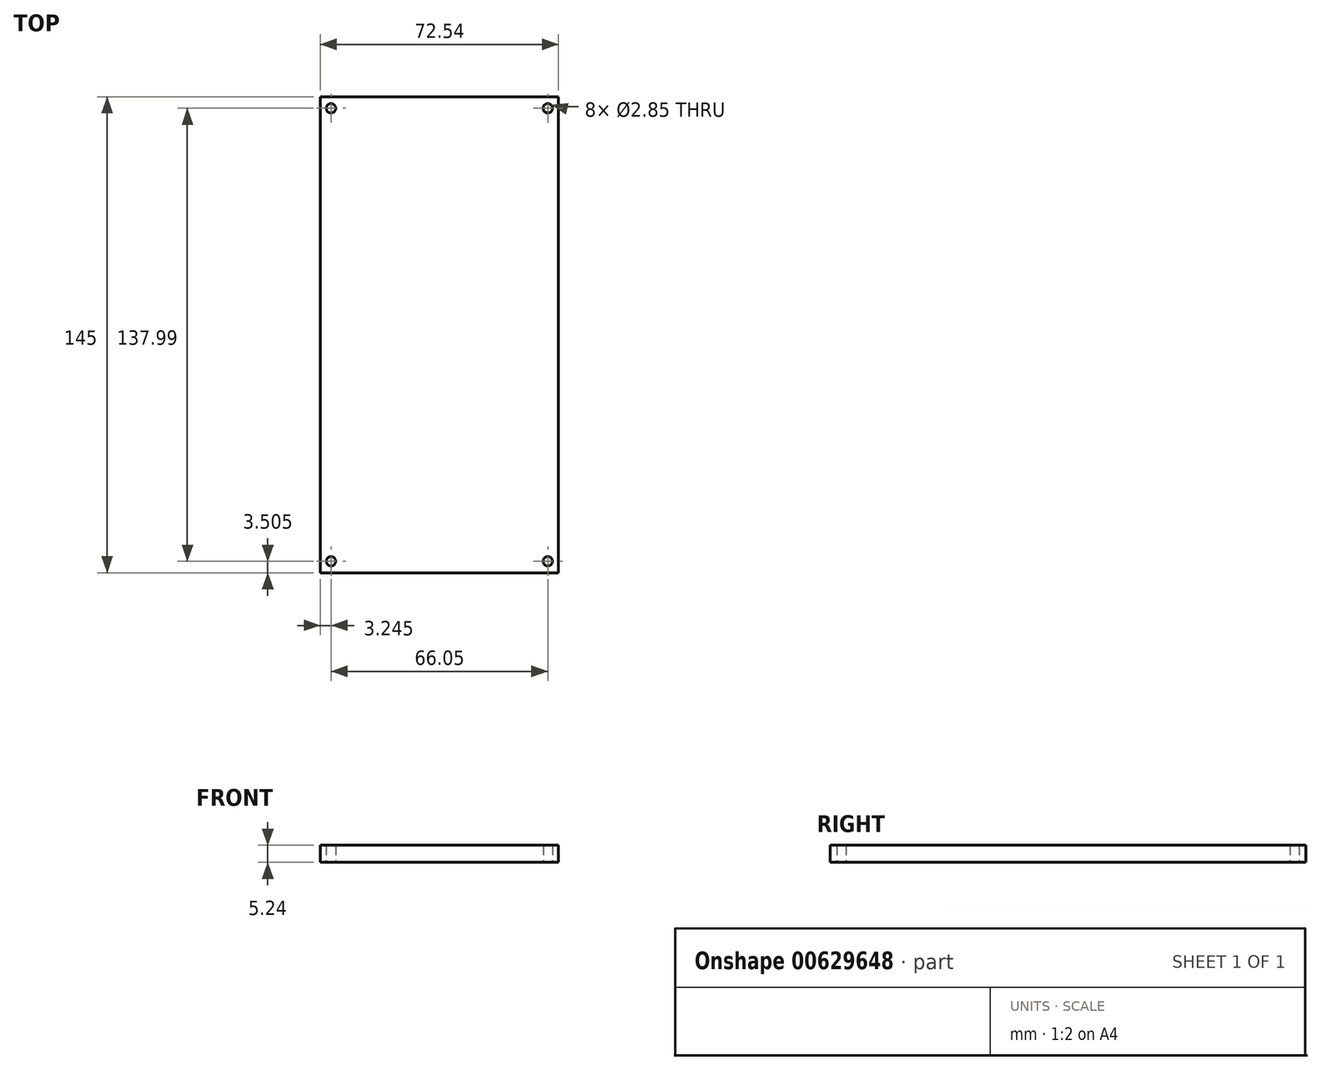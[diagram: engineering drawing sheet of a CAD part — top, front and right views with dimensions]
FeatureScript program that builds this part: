
annotation { "Feature Type Name" : "Feature", "Feature Type Description" : "" }
export const myFeature = defineFeature(function(context is Context, id is Id, definition is map)
    precondition{}
    {
        {
            var Q0;
            Q0=qCreatedBy(makeId("Top.planeOp"),FACE);
            var sketch = newSketch(context, id + "F0", { "sketchPlane" : qUnion([Q0])});
            skLineSegment(sketch, "E0.bottom", {"start": v(-36.27, -72.5) * mm, "end": v(-36.27, 72.5) * mm});
            skLineSegment(sketch, "E0.top", {"start": v(36.27, -72.5) * mm, "end": v(36.27, 72.5) * mm});
            skLineSegment(sketch, "E0.left", {"start": v(-36.27, -72.5) * mm, "end": v(36.27, -72.5) * mm});
            skLineSegment(sketch, "E0.right", {"start": v(-36.27, 72.5) * mm, "end": v(36.27, 72.5) * mm});
            skPoint(sketch, "E0.middle", {"position": v(0, 0) * mm});
            skPoint(sketch, "E1", {"position": v(0, 72.5) * mm});
            skPoint(sketch, "E2", {"position": v(36.27, 0) * mm});
            skCircle(sketch, "E3", {"center": v(33.03, 69) * mm, "radius": 1.43 * mm});
            skCircle(sketch, "E4", {"center": v(-33.03, 69) * mm, "radius": 1.43 * mm});
            skCircle(sketch, "E5", {"center": v(33.03, -69) * mm, "radius": 1.43 * mm});
            skCircle(sketch, "E6", {"center": v(-33.03, -69) * mm, "radius": 1.43 * mm});
            skSolve(sketch);
        }
        {
            var Q0;
            Q0=qSketchRegion(id+"F0",true);
            extrude(context, id + "F1", {"entities" : qUnion([Q0]), "depth" : 5.24 * mm});
        }
    });
